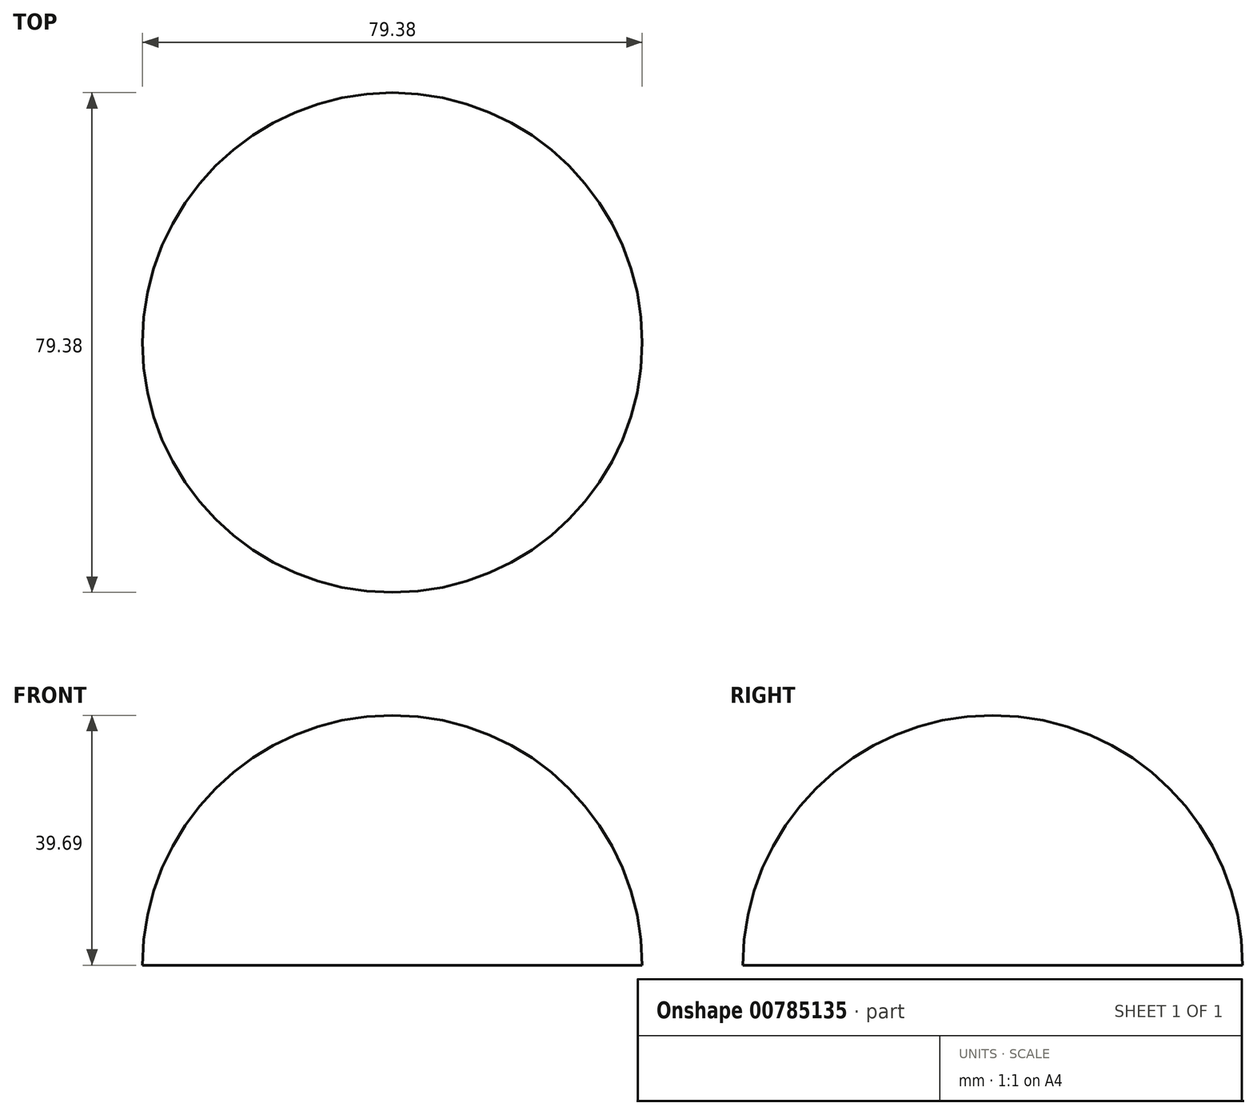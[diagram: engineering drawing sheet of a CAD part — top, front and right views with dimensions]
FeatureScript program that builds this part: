
annotation { "Feature Type Name" : "Feature", "Feature Type Description" : "" }
export const myFeature = defineFeature(function(context is Context, id is Id, definition is map)
    precondition{}
    {
        {
            var Q0;
            Q0=qCreatedBy(makeId("Top.planeOp"),FACE);
            var sketch = newSketch(context, id + "F0", { "sketchPlane" : qUnion([Q0])});
            skCircle(sketch, "E0", {"center": v(0, 0) * mm, "radius": 39.69 * mm});
            skLineSegment(sketch, "E1", {"start": v(0, 39.69) * mm, "end": v(0, -39.69) * mm});
            skSolve(sketch);
        }
        {
            var Q0;
            {var subQ0=sQuery(id+"F0.wireOp",EDGE,"E1");Q0=makeQuery(id+"F0.imprint","IMPRINT",FACE,{"disambiguationData":[TD([[makeQuery(id+"F0.imprint","IMPRINT",EDGE,{"derivedFrom":subQ0}),1.0]])]});}
            var Q1;
            Q1=sQuery(id+"F0.wireOp",EDGE,"E1");
            revolve(context, id + "F1", {"surfaceOperationType" : NewSurfaceOperationType.NEW, "entities" : qUnion([Q0]), "axis" : qUnion([Q1]), "revolveType" : RevolveType.ONE_DIRECTION, "angle" : 180 * degree});
        }
    });
